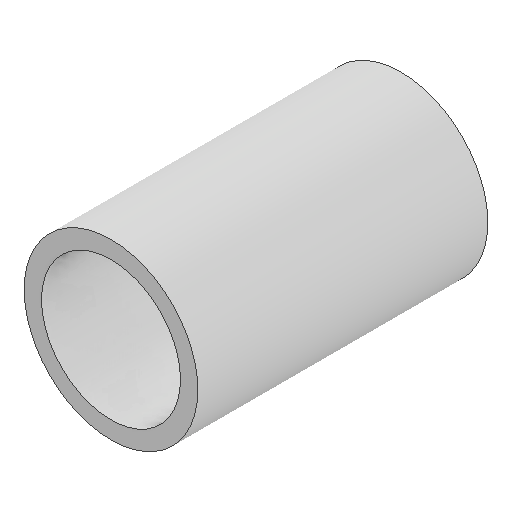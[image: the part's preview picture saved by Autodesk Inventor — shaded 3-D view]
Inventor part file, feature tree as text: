
AUTODESK INVENTOR PART (.ipt)
format: ipt  version: 2025.1 (Build 291241000, 241)  size: 102,912 bytes
history: native  units: mm
features: other x1, extrude x1, sketch x1
ambient origin geometry x8: Origin, YZ Plane, XZ Plane, XY Plane, X Axis, Y Axis, Z Axis, Center Point
bodies: Body1 (feature_tree)
feature tree (3):
  other  "Bryła1"
  extrude  "Wyciągnięcie proste1"  Depth=4.0mm
  sketch  "Szkic1"
